# Revit family: Sanitary_Taps-Mixers_TOTO-USA-Inc_Helix-EcoPower-Faucet-0-5-GPM
name_source: partatom
category: Plumbing Fixtures
revit_build: Autodesk Revit 2015 (Build: 20140606_1530(x64)
units: mm (PartAtom-declared; Revit-internal decimal feet)

## types (1)
- TELS115
    BIMobject category = Taps & Mixers
    BIMobject category code = sanitary-taps-mixers
    BIMobject main category = Sanitary
    BIMobject main category code = sanitary
    Brand url = https://www.totousa.com
    Default Elevation = 4' - 0"
    Edition number = 1
    IFC Classification = Sanitary Terminal
    Installation instructions = https://www.totousa.com
    Manufacturer name = TOTO USA Inc
    Masterformat 2014 Code = 10 28 00
    Masterformat 2014 Description = Toilet, Bath, and Laundry Accessories
    Material = <By Category>
    Material main = Polished Chrome
    NBS Reference Code = 35-06-07
    NBS Reference Description = Bath Water Supply Fittings
    Nominal height = 0' - 0"
    Nominal width = 0' - 0"
    OmniClass Code = 23-31 11 00
    OmniClass Description = Faucets
    Product Guid = a5606b2f-feff-4fd9-b337-6f3df5532b4f
    Product SKU = toto-tel125-d10e
    Product certification = https://www.totousa.com
    Product data url = https://bimobject.com
    Product family = Single Faucets
    Product group = Helix??
    Product url = https://www.totousa.com
    QR code = http://bimobject.com
    Technical description = https://www.totousa.com
    UNSPSC Code = 30181505
    Uniclass 1.4 Code = L725111
    Uniclass 1.4 Description = Mixer taps
    Uniclass 2.0 Code = PR-35-06-07
    Uniclass 2.0 Description = Bath Water Supply Fittings
    Uniclass 2015 Code = Pr_40_20_87_84
    Uniclass 2015 Name = Sink taps
    Uniformat II Code = D2030
    Uniformat II Description = Sanitary Waste
    Youtube clip = https://youtu.be

## geometry (parser evidence)
native form markers: Blend x4, Sweep x2
no freeform markers — native parametric forms only
